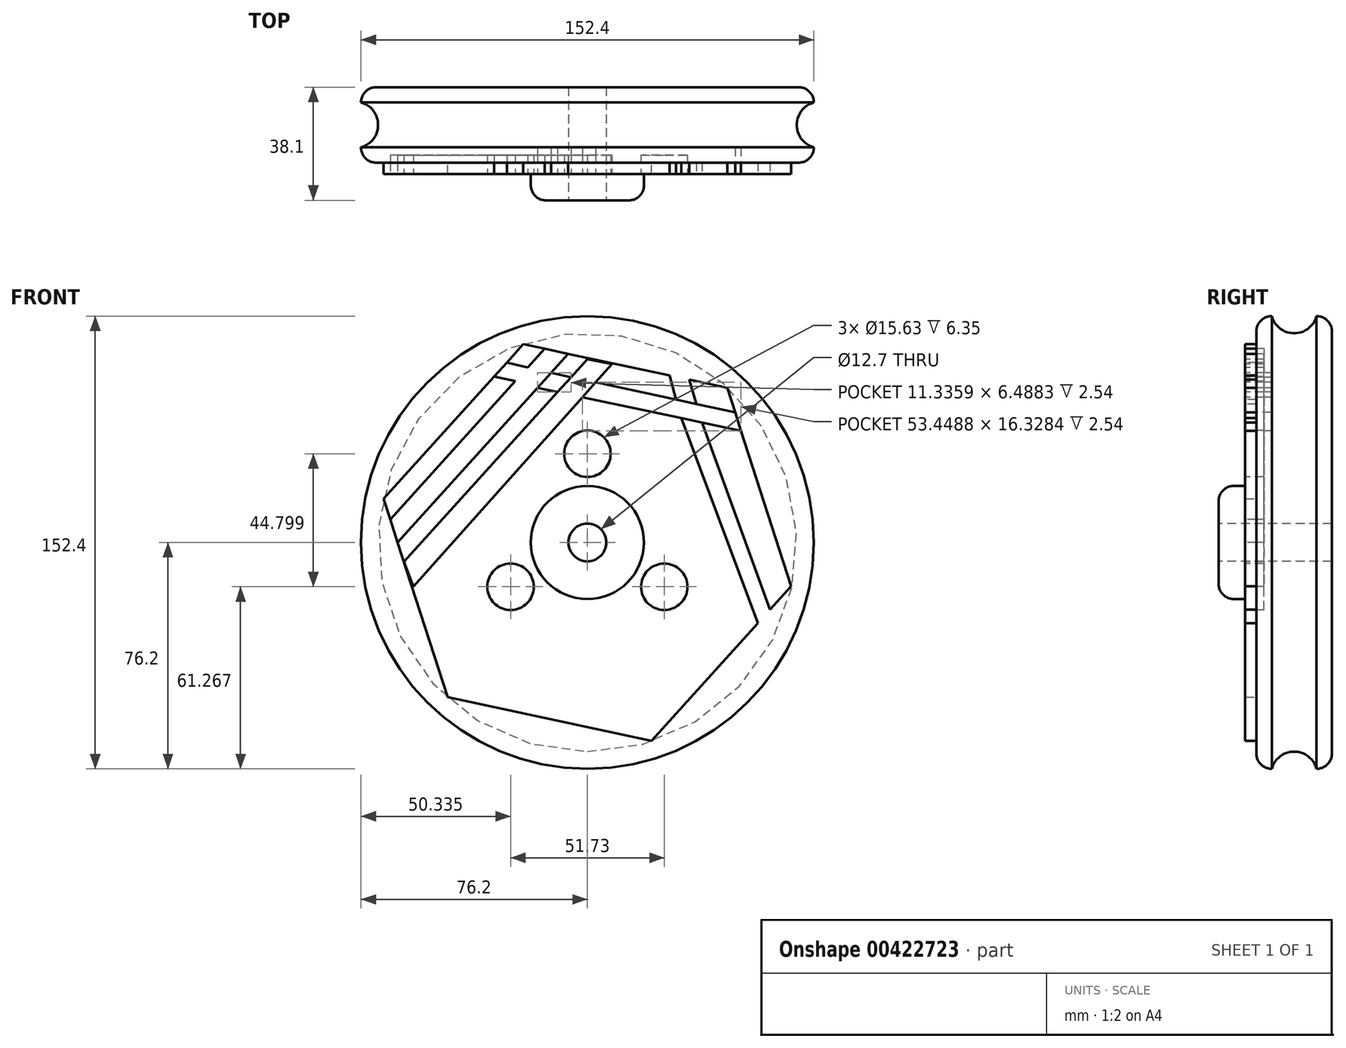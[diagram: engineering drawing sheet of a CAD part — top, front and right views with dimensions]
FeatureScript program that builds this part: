
annotation { "Feature Type Name" : "Feature", "Feature Type Description" : "" }
export const myFeature = defineFeature(function(context is Context, id is Id, definition is map)
    precondition{}
    {
        {
            var Q0;
            Q0=qCreatedBy(makeId("Front.planeOp"),FACE);
            var sketch = newSketch(context, id + "F0", { "sketchPlane" : qUnion([Q0])});
            skCircle(sketch, "E0", {"center": v(0, 0) * mm, "radius": 76.2 * mm});
            skSolve(sketch);
        }
        {
            var Q0;
            Q0=makeQuery(id+"F0.imprint","IMPRINT",FACE,{"disambiguationData":[TD([[makeQuery(id+"F0.imprint","IMPRINT",EDGE,{"derivedFrom":sQuery(id+"F0.wireOp",EDGE,"E0")}),1.0]])]});
            extrude(context, id + "F1", {"entities" : qUnion([Q0]), "depth" : 25.4 * mm, "offsetDistance" : 25.4 * mm});
        }
        {
            var Q0;
            Q0=makeQuery(id+"F1.opExtrude","CAP_EDGE",EDGE,{"disambiguationData":[OSD([sQuery(id+"F0.wireOp",EDGE,"E0")])],"isStart":true});
            var Q1;
            Q1=makeQuery(id+"F1.opExtrude","CAP_EDGE",EDGE,{"disambiguationData":[OSD([sQuery(id+"F0.wireOp",EDGE,"E0")])],"isStart":false});
            fillet(context, id + "F2", {"entities" : qUnion([Q0, Q1]), "radius" : 5.08 * mm, "tangentPropagation" : true, "allowEdgeOverflow" : false});
        }
        {
            var Q0;
            Q0=makeQuery(id+"F1.opExtrude","CAP_FACE",FACE,{"disambiguationData":[OSD([sQuery(id+"F0.wireOp",EDGE,"E0")])],"isStart":false});
            var sketch = newSketch(context, id + "F3", { "sketchPlane" : qUnion([Q0])});
            skCircle(sketch, "E1", {"center": v(0, 0) * mm, "radius": 19.05 * mm});
            skSolve(sketch);
        }
        {
            var Q0;
            Q0=makeQuery(id+"F3.imprint","IMPRINT",FACE,{"disambiguationData":[TD([[makeQuery(id+"F3.imprint","IMPRINT",EDGE,{"derivedFrom":sQuery(id+"F3.wireOp",EDGE,"E1")}),1.0]])]});
            extrude(context, id + "F4", {"entities" : qUnion([Q0]), "operationType" : NewBodyOperationType.ADD, "depth" : 12.7 * mm, "offsetDistance" : 25.4 * mm});
        }
        {
            var Q0;
            Q0=makeQuery(id+"F4.opExtrude","CAP_FACE",FACE,{"disambiguationData":[OSD([sQuery(id+"F3.wireOp",EDGE,"E1")])],"isStart":false});
            fillet(context, id + "F5", {"entities" : qUnion([Q0]), "radius" : 5.08 * mm, "tangentPropagation" : true, "allowEdgeOverflow" : false});
        }
        {
            var Q0;
            Q0=makeQuery(id+"F4.opExtrude","CAP_FACE",FACE,{"disambiguationData":[OSD([sQuery(id+"F3.wireOp",EDGE,"E1")])],"isStart":false});
            var sketch = newSketch(context, id + "F6", { "sketchPlane" : qUnion([Q0])});
            skCircle(sketch, "E2", {"center": v(0, 0) * mm, "radius": 6.35 * mm});
            skSolve(sketch);
        }
        {
            var Q0;
            Q0=makeQuery(id+"F6.imprint","IMPRINT",FACE,{"disambiguationData":[TD([[makeQuery(id+"F6.imprint","IMPRINT",EDGE,{"derivedFrom":sQuery(id+"F6.wireOp",EDGE,"E2")}),1.0]])]});
            extrude(context, id + "F7", {"entities" : qUnion([Q0]), "operationType" : NewBodyOperationType.REMOVE, "oppositeDirection" : true, "depth" : 76.2 * mm, "offsetDistance" : 25.4 * mm});
        }
        {
            var Q0;
            Q0=qCreatedBy(makeId("Right.planeOp"),FACE);
            var sketch = newSketch(context, id + "F8", { "sketchPlane" : qUnion([Q0])});
            skCircle(sketch, "E3", {"center": v(-12.7, 78.25) * mm, "radius": 7.82 * mm});
            skPoint(sketch, "E3.first.point", {"position": v(-20.24, 76.23) * mm});
            skPoint(sketch, "E3.second.point", {"position": v(-5.12, 76.27) * mm});
            skPoint(sketch, "E3.third.point", {"position": v(-12.28, 70.44) * mm});
            skSolve(sketch);
        }
        {
            var Q0;
            Q0=makeQuery(id+"F8.imprint","IMPRINT",FACE,{"disambiguationData":[TD([[makeQuery(id+"F8.imprint","IMPRINT",EDGE,{"derivedFrom":sQuery(id+"F8.wireOp",EDGE,"E3")}),1.0]])]});
            var Q1;
            {var subQ0=sQuery(id+"F0.wireOp",EDGE,"E0");Q1=makeQuery(id+"F2.opFillet","BLEND_EDGE",EDGE,{"blendedFrom":[makeQuery(id+"F1.opExtrude","CAP_EDGE",EDGE,{"disambiguationData":[OSD([subQ0])],"isStart":false}),makeQuery(id+"F1.opExtrude","CAP_FACE",FACE,{"disambiguationData":[OSD([subQ0])],"isStart":false})],"blendedInto":[makeQuery(id+"F1.opExtrude","CAP_FACE",FACE,{"disambiguationData":[OSD([subQ0])],"isStart":false})]});}
            revolve(context, id + "F9", {"operationType" : NewBodyOperationType.REMOVE, "entities" : qUnion([Q0]), "axis" : qUnion([Q1]), "revolveType" : RevolveType.FULL, "oppositeDirection" : true});
        }
        {
            var Q0;
            Q0=makeQuery(id+"F1.opExtrude","CAP_FACE",FACE,{"disambiguationData":[OSD([sQuery(id+"F0.wireOp",EDGE,"E0")])],"isStart":false});
            var sketch = newSketch(context, id + "F10", { "sketchPlane" : qUnion([Q0])});
            skCircle(sketch, "E4.cCircle", {"center": v(0, 0) * mm, "radius": 60.77 * mm, "construction": true});
            skLineSegment(sketch, "E4.0", {"start": v(-21.57, 66.77) * mm, "end": v(47.04, 52.07) * mm});
            skLineSegment(sketch, "E4.1", {"start": v(47.04, 52.07) * mm, "end": v(68.61, -14.7) * mm});
            skLineSegment(sketch, "E4.2", {"start": v(68.61, -14.7) * mm, "end": v(21.57, -66.77) * mm});
            skLineSegment(sketch, "E4.3", {"start": v(21.57, -66.77) * mm, "end": v(-47.04, -52.07) * mm});
            skLineSegment(sketch, "E4.4", {"start": v(-47.04, -52.07) * mm, "end": v(-68.61, 14.7) * mm});
            skLineSegment(sketch, "E4.5", {"start": v(-68.61, 14.7) * mm, "end": v(-21.57, 66.77) * mm});
            skPoint(sketch, "E4.0.midPoint", {"position": v(12.73, 59.42) * mm});
            skSolve(sketch);
        }
        {
            var Q0;
            Q0=makeQuery(id+"F10.imprint","IMPRINT",FACE,{"disambiguationData":[TD([[makeQuery(id+"F10.imprint","IMPRINT",EDGE,{"derivedFrom":sQuery(id+"F10.wireOp",EDGE,"E4.0")}),1.0]])]});
            var sketch = newSketch(context, id + "F11", { "sketchPlane" : qUnion([Q0])});
            skSolve(sketch);
        }
        {
            var Q0;
            Q0 = qSketchRegion(id + "F11", true);
            var Q1;
            Q1=makeQuery(id+"F10.imprint","IMPRINT",FACE,{"disambiguationData":[TD([[makeQuery(id+"F10.imprint","IMPRINT",EDGE,{"derivedFrom":sQuery(id+"F10.wireOp",EDGE,"E4.0")}),-1.0]])]});
            extrude(context, id + "F12", {"entities" : qUnion([Q0, Q1]), "operationType" : NewBodyOperationType.ADD, "depth" : 3.8 * mm, "offsetDistance" : 25.4 * mm});
        }
        {
            var Q0;
            Q0=makeQuery(id+"F12.opExtrude","CAP_FACE",FACE,{"disambiguationData":[OSD([sQuery(id+"F3.wireOp",EDGE,"E1"),sQuery(id+"F10.wireOp",EDGE,"E4.0"),sQuery(id+"F10.wireOp",EDGE,"E4.1"),sQuery(id+"F10.wireOp",EDGE,"E4.2"),sQuery(id+"F10.wireOp",EDGE,"E4.3"),sQuery(id+"F10.wireOp",EDGE,"E4.4"),sQuery(id+"F10.wireOp",EDGE,"E4.5")])],"isStart":false});
            var sketch = newSketch(context, id + "F13", { "sketchPlane" : qUnion([Q0])});
            skCircle(sketch, "E5", {"center": v(0, 29.87) * mm, "radius": 7.82 * mm});
            skCircle(sketch, "E6.1.0", {"center": v(25.86, -14.93) * mm, "radius": 7.82 * mm});
            skCircle(sketch, "E6.2.0", {"center": v(-25.86, -14.93) * mm, "radius": 7.82 * mm});
            skPoint(sketch, "E6.center", {"position": v(0, 0) * mm});
            skLineSegment(sketch, "E6.anchor1", {"start": v(0, 0) * mm, "end": v(0, 29.87) * mm, "construction": true});
            skLineSegment(sketch, "E6.anchor2", {"start": v(0, 0) * mm, "end": v(-25.86, -14.93) * mm, "construction": true});
            skSolve(sketch);
        }
        {
            var Q0;
            Q0=makeQuery(id+"F13.imprint","IMPRINT",FACE,{"disambiguationData":[TD([[makeQuery(id+"F13.imprint","IMPRINT",EDGE,{"derivedFrom":sQuery(id+"F13.wireOp",EDGE,"E6.2.0")}),1.0]])]});
            var Q1;
            Q1=makeQuery(id+"F13.imprint","IMPRINT",FACE,{"disambiguationData":[TD([[makeQuery(id+"F13.imprint","IMPRINT",EDGE,{"derivedFrom":sQuery(id+"F13.wireOp",EDGE,"E6.1.0")}),1.0]])]});
            var Q2;
            Q2=makeQuery(id+"F13.imprint","IMPRINT",FACE,{"disambiguationData":[TD([[makeQuery(id+"F13.imprint","IMPRINT",EDGE,{"derivedFrom":sQuery(id+"F13.wireOp",EDGE,"E5")}),1.0]])]});
            extrude(context, id + "F14", {"entities" : qUnion([Q0, Q1, Q2]), "operationType" : NewBodyOperationType.REMOVE, "oppositeDirection" : true, "depth" : 6.35 * mm, "offsetDistance" : 25.4 * mm});
        }
        {
            var Q0;
            Q0=makeQuery(id+"F12.opExtrude","CAP_FACE",FACE,{"disambiguationData":[OSD([sQuery(id+"F3.wireOp",EDGE,"E1"),sQuery(id+"F10.wireOp",EDGE,"E4.0"),sQuery(id+"F10.wireOp",EDGE,"E4.1"),sQuery(id+"F10.wireOp",EDGE,"E4.2"),sQuery(id+"F10.wireOp",EDGE,"E4.3"),sQuery(id+"F10.wireOp",EDGE,"E4.4"),sQuery(id+"F10.wireOp",EDGE,"E4.5")])],"isStart":false});
            var sketch = newSketch(context, id + "F15", { "sketchPlane" : qUnion([Q0])});
            skLineSegment(sketch, "E7", {"start": v(-14.4, 65.23) * mm, "end": v(-66.36, 7.72) * mm});
            skLineSegment(sketch, "E8", {"start": v(-66.36, 7.72) * mm, "end": v(-63.86, 0) * mm});
            skLineSegment(sketch, "E9", {"start": v(-63.86, 0) * mm, "end": v(-6.47, 63.53) * mm});
            skSolve(sketch);
        }
        {
            var Q0;
            {var subQ3=sQuery(id+"F15.wireOp",EDGE,"E9");Q0=makeQuery(id+"F15.imprint","IMPRINT",FACE,{"disambiguationData":[TD([[makeQuery(id+"F15.imprint","IMPRINT",EDGE,{"derivedFrom":subQ3}),-1.0]])]});}
            var sketch = newSketch(context, id + "F16", { "sketchPlane" : qUnion([Q0])});
            skLineSegment(sketch, "E10", {"start": v(-61.73, -6.48) * mm, "end": v(0, 61.73) * mm});
            skLineSegment(sketch, "E11", {"start": v(0, 61.73) * mm, "end": v(8.2, 60) * mm});
            skLineSegment(sketch, "E12", {"start": v(8.2, 60) * mm, "end": v(-58.57, -14.82) * mm});
            skLineSegment(sketch, "E13", {"start": v(-58.57, -14.82) * mm, "end": v(-61.73, -6.48) * mm});
            skSolve(sketch);
        }
        {
            var Q0;
            {var subQ0=sQuery(id+"F15.wireOp",EDGE,"E7");Q0=makeQuery(id+"F15.imprint","IMPRINT",FACE,{"disambiguationData":[TD([[makeQuery(id+"F15.imprint","IMPRINT",EDGE,{"derivedFrom":subQ0}),1.0]])]});}
            var Q1;
            Q1=makeQuery(id+"F16.imprint","IMPRINT",FACE,{"disambiguationData":[TD([[makeQuery(id+"F16.imprint","IMPRINT",EDGE,{"derivedFrom":sQuery(id+"F16.wireOp",EDGE,"E10")}),-1.0]])]});
            extrude(context, id + "F17", {"entities" : qUnion([Q0, Q1]), "operationType" : NewBodyOperationType.REMOVE, "oppositeDirection" : true, "depth" : 6.35 * mm, "offsetDistance" : 25.4 * mm});
        }
        {
            var Q0;
            {var subQ0=sQuery(id+"F10.wireOp",EDGE,"E4.3");var subQ1=sQuery(id+"F10.wireOp",EDGE,"E4.4");var subQ2=sQuery(id+"F3.wireOp",EDGE,"E1");var subQ3=sQuery(id+"F10.wireOp",EDGE,"E4.1");var subQ4=sQuery(id+"F10.wireOp",EDGE,"E4.0");var subQ5=sQuery(id+"F10.wireOp",EDGE,"E4.2");Q0=makeQuery(id+"F17.boolean.opBoolean","SPLIT",FACE,{"disambiguationData":[TD([makeQuery(id+"F4.opExtrude","SWEPT_FACE",FACE,{"disambiguationData":[OSD([subQ2])]})])],"derivedFrom":makeQuery(id+"F12.opExtrude","CAP_FACE",FACE,{"disambiguationData":[OSD([subQ2,subQ4,subQ3,subQ5,subQ0,subQ1,sQuery(id+"F10.wireOp",EDGE,"E4.5")])],"isStart":false})});}
            var sketch = newSketch(context, id + "F18", { "sketchPlane" : qUnion([Q0])});
            skLineSegment(sketch, "E14", {"start": v(-12.26, 57.12) * mm, "end": v(49.7, 43.85) * mm});
            skLineSegment(sketch, "E15", {"start": v(49.7, 43.85) * mm, "end": v(51.72, 37.58) * mm});
            skLineSegment(sketch, "E16", {"start": v(51.72, 37.58) * mm, "end": v(-16.82, 52.07) * mm});
            skLineSegment(sketch, "E17", {"start": v(-16.82, 52.07) * mm, "end": v(-12.26, 57.12) * mm});
            skSolve(sketch);
        }
        {
            var Q0;
            {var subQ0=sQuery(id+"F18.wireOp",EDGE,"E17");Q0=makeQuery(id+"F18.imprint","IMPRINT",FACE,{"disambiguationData":[TD([[makeQuery(id+"F18.imprint","IMPRINT",EDGE,{"derivedFrom":subQ0}),-1.0]])]});}
            var Q1;
            {var subQ0=sQuery(id+"F18.wireOp",EDGE,"E15");Q1=makeQuery(id+"F18.imprint","IMPRINT",FACE,{"disambiguationData":[TD([[makeQuery(id+"F18.imprint","IMPRINT",EDGE,{"derivedFrom":subQ0}),-1.0]])]});}
            extrude(context, id + "F19", {"entities" : qUnion([Q0, Q1]), "operationType" : NewBodyOperationType.REMOVE, "oppositeDirection" : true, "depth" : 8.9 * mm, "offsetDistance" : 25.4 * mm});
        }
        {
            var Q0;
            {var subQ0=sQuery(id+"F10.wireOp",EDGE,"E4.0");var subQ1=sQuery(id+"F10.wireOp",EDGE,"E4.4");var subQ2=sQuery(id+"F10.wireOp",EDGE,"E4.5");Q0=makeQuery(id+"F17.boolean.opBoolean","SPLIT",FACE,{"disambiguationData":[TD([makeQuery(id+"F12.opExtrude","SWEPT_FACE",FACE,{"disambiguationData":[OSD([subQ2])]})])],"derivedFrom":makeQuery(id+"F12.opExtrude","CAP_FACE",FACE,{"disambiguationData":[OSD([sQuery(id+"F3.wireOp",EDGE,"E1"),subQ0,sQuery(id+"F10.wireOp",EDGE,"E4.1"),sQuery(id+"F10.wireOp",EDGE,"E4.2"),sQuery(id+"F10.wireOp",EDGE,"E4.3"),subQ1,subQ2])],"isStart":false})});}
            var sketch = newSketch(context, id + "F20", { "sketchPlane" : qUnion([Q0])});
            skLineSegment(sketch, "E18", {"start": v(-20.07, 58.96) * mm, "end": v(-27.14, 60.6) * mm});
            skLineSegment(sketch, "E19", {"start": v(-27.14, 60.6) * mm, "end": v(-31.37, 55.92) * mm});
            skLineSegment(sketch, "E20", {"start": v(-31.37, 55.92) * mm, "end": v(-24.27, 54.31) * mm});
            skLineSegment(sketch, "E21", {"start": v(-24.27, 54.31) * mm, "end": v(-20.07, 58.96) * mm});
            skSolve(sketch);
        }
        {
            var Q0;
            Q0=makeQuery(id+"F20.imprint","IMPRINT",FACE,{"disambiguationData":[TD([[makeQuery(id+"F20.imprint","IMPRINT",EDGE,{"derivedFrom":sQuery(id+"F20.wireOp",EDGE,"E18")}),1.0]])]});
            extrude(context, id + "F21", {"entities" : qUnion([Q0]), "operationType" : NewBodyOperationType.REMOVE, "oppositeDirection" : true, "depth" : 6.35 * mm, "offsetDistance" : 25.4 * mm});
        }
        {
            var Q0;
            {var subQ4=sQuery(id+"F10.wireOp",EDGE,"E4.3");var subQ9=sQuery(id+"F10.wireOp",EDGE,"E4.4");var subQ11=sQuery(id+"F3.wireOp",EDGE,"E1");var subQ12=makeQuery(id+"F4.opExtrude","SWEPT_FACE",FACE,{"disambiguationData":[OSD([subQ11])]});var subQ13=sQuery(id+"F10.wireOp",EDGE,"E4.1");var subQ15=sQuery(id+"F10.wireOp",EDGE,"E4.2");var subQ21=sQuery(id+"F10.wireOp",EDGE,"E4.0");Q0=makeQuery(id+"F19.boolean.opBoolean","SPLIT",FACE,{"disambiguationData":[TD([subQ12])],"derivedFrom":makeQuery(id+"F17.boolean.opBoolean","SPLIT",FACE,{"disambiguationData":[TD([subQ12])],"derivedFrom":makeQuery(id+"F12.opExtrude","CAP_FACE",FACE,{"disambiguationData":[OSD([subQ11,subQ21,subQ13,subQ15,subQ4,subQ9,sQuery(id+"F10.wireOp",EDGE,"E4.5")])],"isStart":false})})});}
            var sketch = newSketch(context, id + "F22", { "sketchPlane" : qUnion([Q0])});
            skLineSegment(sketch, "E22", {"start": v(31.57, 41.84) * mm, "end": v(57.35, -27.17) * mm});
            skLineSegment(sketch, "E23", {"start": v(57.35, -27.17) * mm, "end": v(61.44, -22.64) * mm});
            skLineSegment(sketch, "E24", {"start": v(61.44, -22.64) * mm, "end": v(38.53, 40.37) * mm});
            skLineSegment(sketch, "E25", {"start": v(38.53, 40.37) * mm, "end": v(31.57, 41.84) * mm});
            skSolve(sketch);
        }
        {
            var Q0;
            Q0=makeQuery(id+"F22.imprint","IMPRINT",FACE,{"disambiguationData":[TD([[makeQuery(id+"F22.imprint","IMPRINT",EDGE,{"derivedFrom":sQuery(id+"F22.wireOp",EDGE,"E22")}),1.0]])]});
            extrude(context, id + "F23", {"entities" : qUnion([Q0]), "operationType" : NewBodyOperationType.REMOVE, "oppositeDirection" : true, "depth" : 3.8 * mm, "offsetDistance" : 25.4 * mm});
        }
        {
            var Q0;
            {var subQ2=sQuery(id+"F10.wireOp",EDGE,"E4.0");var subQ3=makeQuery(id+"F12.opExtrude","SWEPT_FACE",FACE,{"disambiguationData":[OSD([subQ2])]});var subQ6=sQuery(id+"F10.wireOp",EDGE,"E4.1");var subQ12=sQuery(id+"F10.wireOp",EDGE,"E4.3");var subQ13=sQuery(id+"F10.wireOp",EDGE,"E4.4");var subQ14=sQuery(id+"F3.wireOp",EDGE,"E1");var subQ15=sQuery(id+"F10.wireOp",EDGE,"E4.2");Q0=makeQuery(id+"F19.boolean.opBoolean","SPLIT",FACE,{"disambiguationData":[TD([subQ3])],"derivedFrom":makeQuery(id+"F17.boolean.opBoolean","SPLIT",FACE,{"disambiguationData":[TD([makeQuery(id+"F4.opExtrude","SWEPT_FACE",FACE,{"disambiguationData":[OSD([subQ14])]})])],"derivedFrom":makeQuery(id+"F12.opExtrude","CAP_FACE",FACE,{"disambiguationData":[OSD([subQ14,subQ2,subQ6,subQ15,subQ12,subQ13,sQuery(id+"F10.wireOp",EDGE,"E4.5")])],"isStart":false})})});}
            var sketch = newSketch(context, id + "F24", { "sketchPlane" : qUnion([Q0])});
            skLineSegment(sketch, "E26", {"start": v(36.66, 46.64) * mm, "end": v(34.27, 54.8) * mm});
            skLineSegment(sketch, "E27", {"start": v(34.27, 54.8) * mm, "end": v(27.71, 56.2) * mm});
            skLineSegment(sketch, "E28", {"start": v(27.71, 56.2) * mm, "end": v(29.75, 48.12) * mm});
            skLineSegment(sketch, "E29", {"start": v(29.75, 48.12) * mm, "end": v(36.66, 46.64) * mm});
            skSolve(sketch);
        }
        {
            var Q0;
            Q0=makeQuery(id+"F24.imprint","IMPRINT",FACE,{"disambiguationData":[TD([[makeQuery(id+"F24.imprint","IMPRINT",EDGE,{"derivedFrom":sQuery(id+"F24.wireOp",EDGE,"E26")}),1.0]])]});
            extrude(context, id + "F25", {"entities" : qUnion([Q0]), "operationType" : NewBodyOperationType.REMOVE, "oppositeDirection" : true, "depth" : 3.8 * mm, "offsetDistance" : 25.4 * mm});
        }
    });
